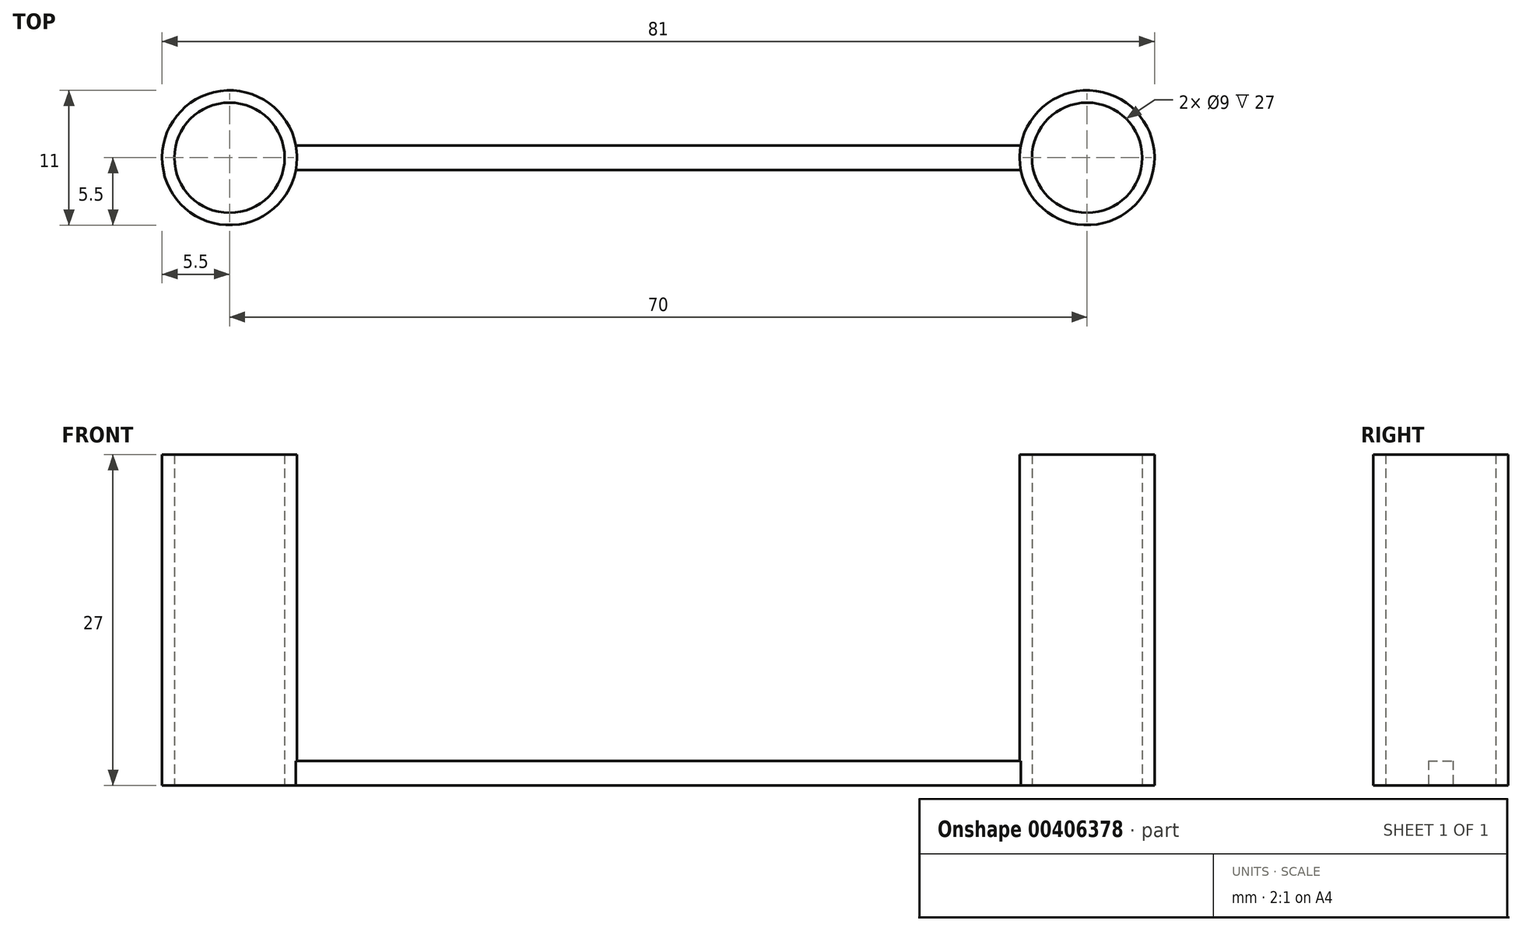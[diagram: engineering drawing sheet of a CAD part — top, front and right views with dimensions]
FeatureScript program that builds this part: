
annotation { "Feature Type Name" : "Feature", "Feature Type Description" : "" }
export const myFeature = defineFeature(function(context is Context, id is Id, definition is map)
    precondition{}
    {
        {
            var Q0;
            Q0=qCreatedBy(makeId("Top.planeOp"),FACE);
            var sketch = newSketch(context, id + "F0", { "sketchPlane" : qUnion([Q0])});
            skCircle(sketch, "E0", {"center": v(-35, 0) * mm, "radius": 4.5 * mm});
            skCircle(sketch, "E1.0", {"center": v(-35, 0) * mm, "radius": 5.5 * mm});
            skLineSegment(sketch, "E2", {"start": v(0, 1) * mm, "end": v(-29.6, 1) * mm});
            skLineSegment(sketch, "E3", {"start": v(0, -1) * mm, "end": v(-29.6, -1) * mm});
            skLineSegment(sketch, "E4", {"start": v(0, 1) * mm, "end": v(0, -1) * mm});
            skSolve(sketch);
        }
        {
            var Q0;
            Q0=makeQuery(id+"F0.imprint","IMPRINT",FACE,{"disambiguationData":[TD([[makeQuery(id+"F0.imprint","IMPRINT",EDGE,{"derivedFrom":sQuery(id+"F0.wireOp",EDGE,"E0")}),-1.0]])]});
            extrude(context, id + "F1", {"entities" : qUnion([Q0]), "depth" : 27 * mm});
        }
        {
            var Q0;
            {var subQ0=sQuery(id+"F0.wireOp",EDGE,"E2");Q0=makeQuery(id+"F0.imprint","IMPRINT",FACE,{"disambiguationData":[TD([[makeQuery(id+"F0.imprint","IMPRINT",EDGE,{"derivedFrom":subQ0}),1.0]])]});}
            extrude(context, id + "F2", {"entities" : qUnion([Q0]), "operationType" : NewBodyOperationType.ADD, "depth" : 2 * mm});
        }
        {
            var Q0;
            Q0=makeQuery(id+"F1.opExtrude","SWEPT_BODY",BODY,{"disambiguationData":[OSD([sQuery(id+"F0.wireOp",EDGE,"E0"),sQuery(id+"F0.wireOp",EDGE,"E1.0")])]});
            var Q1;
            Q1=qCreatedBy(makeId("Right.planeOp"),FACE);
            mirror(context, id + "F3", {"operationType" : NewBodyOperationType.ADD, "entities" : qUnion([Q0]), "mirrorPlane" : qUnion([Q1])});
        }
    });
